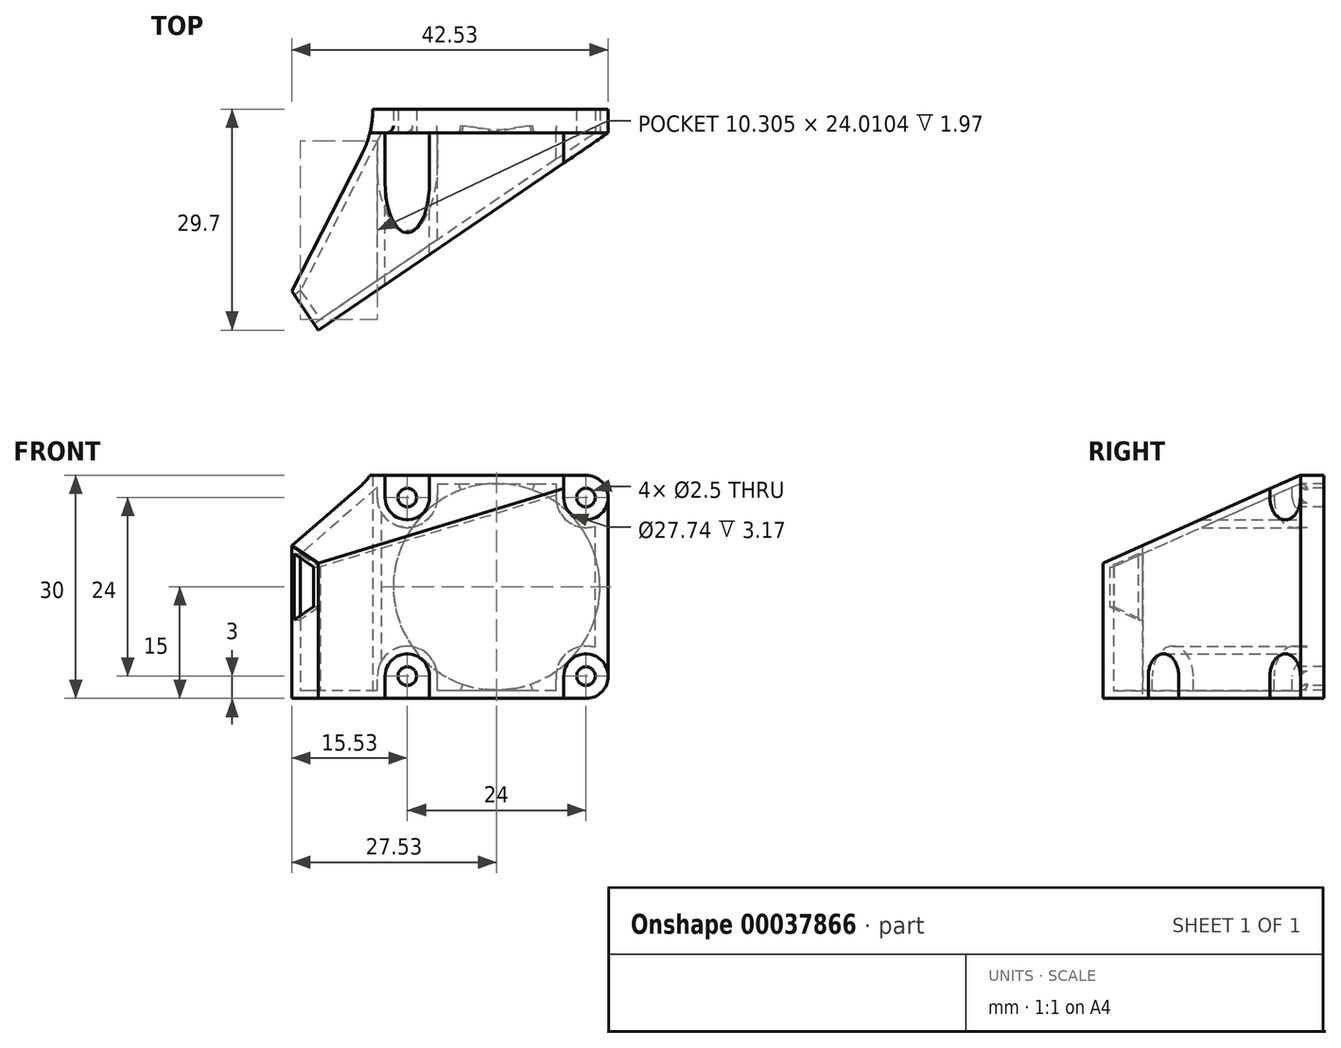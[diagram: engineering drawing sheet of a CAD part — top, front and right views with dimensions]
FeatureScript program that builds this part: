
annotation { "Feature Type Name" : "Feature", "Feature Type Description" : "" }
export const myFeature = defineFeature(function(context is Context, id is Id, definition is map)
    precondition{}
    {
        {
            var Q0;
            Q0=qCreatedBy(makeId("Top.planeOp"),FACE);
            var sketch = newSketch(context, id + "F0", { "sketchPlane" : qUnion([Q0])});
            skLineSegment(sketch, "E0", {"start": v(30, -3.17) * mm, "end": v(-8.96, -29.7) * mm});
            skLineSegment(sketch, "E1", {"start": v(30, 0) * mm, "end": v(0, 0) * mm, "construction": true});
            skLineSegment(sketch, "E2", {"start": v(-1.63, -3.17) * mm, "end": v(-12.53, -24.44) * mm});
            skLineSegment(sketch, "E3", {"start": v(30, 0) * mm, "end": v(30, -3.17) * mm, "construction": true});
            skLineSegment(sketch, "E4", {"start": v(-8.96, -29.7) * mm, "end": v(-12.53, -24.44) * mm});
            skLineSegment(sketch, "E5", {"start": v(30, -3.17) * mm, "end": v(-1.63, -3.17) * mm});
            skLineSegment(sketch, "E6", {"start": v(0, 0) * mm, "end": v(-1.63, -3.17) * mm, "construction": true});
            skSolve(sketch);
        }
        {
            var Q0;
            Q0 = qSketchRegion(id + "F0", true);
            extrude(context, id + "F1", {"entities" : qUnion([Q0]), "depth" : 30 * mm});
        }
        {
            var Q0;
            Q0=qCreatedBy(makeId("Right.planeOp"),FACE);
            var sketch = newSketch(context, id + "F2", { "sketchPlane" : qUnion([Q0])});
            skLineSegment(sketch, "E7.bottom", {"start": v(-3.18, 30) * mm, "end": v(-29.7, 30) * mm});
            skLineSegment(sketch, "E7.top", {"start": v(-3.18, 18.17) * mm, "end": v(-29.7, 18.17) * mm, "construction": true});
            skLineSegment(sketch, "E7.left", {"start": v(-3.18, 30) * mm, "end": v(-3.18, 18.18) * mm, "construction": true});
            skLineSegment(sketch, "E7.right", {"start": v(-29.7, 30) * mm, "end": v(-29.7, 18.17) * mm});
            skLineSegment(sketch, "E8.bottom", {"start": v(-3.18, 0) * mm, "end": v(-29.7, 0) * mm});
            skLineSegment(sketch, "E8.top", {"start": v(-3.18, 11.82) * mm, "end": v(-29.7, 11.82) * mm, "construction": true});
            skLineSegment(sketch, "E8.left", {"start": v(-3.18, 0) * mm, "end": v(-3.18, 11.82) * mm, "construction": true});
            skLineSegment(sketch, "E8.right", {"start": v(-29.7, 0) * mm, "end": v(-29.7, 11.82) * mm});
            skLineSegment(sketch, "E9", {"start": v(-3.18, 30) * mm, "end": v(-29.7, 18.17) * mm});
            skLineSegment(sketch, "E10", {"start": v(-29.7, 11.83) * mm, "end": v(-3.18, 0) * mm});
            skSolve(sketch);
        }
        {
            var Q0;
            Q0 = qSketchRegion(id + "F2", true);
            var Q1;
            Q1=makeQuery(id+"F1.opExtrude","SWEPT_FACE",FACE,{"disambiguationData":[OSD([sQuery(id+"F0.wireOp",EDGE,"E0")])]});
            var Q2;
            Q2=makeQuery(id+"F1.opExtrude","SWEPT_FACE",FACE,{"disambiguationData":[OSD([sQuery(id+"F0.wireOp",EDGE,"E2")])]});
            extrude(context, id + "F3", {"entities" : qUnion([Q0]), "operationType" : NewBodyOperationType.REMOVE, "endBound" : BoundingType.UP_TO_SURFACE, "endBoundEntityFace" : qUnion([Q1]), "depth" : 25.4 * mm, "hasSecondDirection" : true, "secondDirectionBound" : SecondDirectionBoundingType.UP_TO_SURFACE, "secondDirectionOppositeDirection" : true, "secondDirectionBoundEntityFace" : qUnion([Q2]), "secondDirectionDepth" : 25.4 * mm});
        }
        {
            var Q0;
            Q0=makeQuery(id+"F1.opExtrude","SWEPT_FACE",FACE,{"disambiguationData":[OSD([sQuery(id+"F0.wireOp",EDGE,"E5")])]});
            var sketch = newSketch(context, id + "F4", { "sketchPlane" : qUnion([Q0])});
            skLineSegment(sketch, "E11.bottom", {"start": v(-30, 0) * mm, "end": v(-24, 0) * mm});
            skLineSegment(sketch, "E11.top", {"start": v(-30, 3) * mm, "end": v(-24, 3) * mm, "construction": true});
            skLineSegment(sketch, "E11.left", {"start": v(-30, 0) * mm, "end": v(-30, 3) * mm});
            skLineSegment(sketch, "E11.right", {"start": v(-24, 0) * mm, "end": v(-24, 3) * mm});
            skLineSegment(sketch, "E12.bottom", {"start": v(-30, 30) * mm, "end": v(-24, 30) * mm});
            skLineSegment(sketch, "E12.top", {"start": v(-30, 27) * mm, "end": v(-24, 27) * mm, "construction": true});
            skLineSegment(sketch, "E12.left", {"start": v(-30, 30) * mm, "end": v(-30, 27) * mm});
            skLineSegment(sketch, "E12.right", {"start": v(-24, 30) * mm, "end": v(-24, 27) * mm});
            skLineSegment(sketch, "E13.bottom", {"start": v(-27, 27) * mm, "end": v(-3, 27) * mm, "construction": true});
            skLineSegment(sketch, "E13.top", {"start": v(-27, 3) * mm, "end": v(-3, 3) * mm, "construction": true});
            skLineSegment(sketch, "E13.left", {"start": v(-27, 27) * mm, "end": v(-27, 3) * mm, "construction": true});
            skLineSegment(sketch, "E13.right", {"start": v(-3, 27) * mm, "end": v(-3, 3) * mm, "construction": true});
            skPoint(sketch, "E14.rect.middle", {"position": v(-3, 3) * mm});
            skPoint(sketch, "E15.rect.middle", {"position": v(-3, 27) * mm});
            skLineSegment(sketch, "E16.bottom", {"start": v(0, 30) * mm, "end": v(-6, 30) * mm});
            skLineSegment(sketch, "E16.top", {"start": v(0, 27) * mm, "end": v(-6, 27) * mm, "construction": true});
            skLineSegment(sketch, "E16.left", {"start": v(0, 30) * mm, "end": v(0, 27) * mm});
            skLineSegment(sketch, "E16.right", {"start": v(-6, 30) * mm, "end": v(-6, 27) * mm});
            skLineSegment(sketch, "E17.bottom", {"start": v(0, 0) * mm, "end": v(-6, 0) * mm});
            skLineSegment(sketch, "E17.top", {"start": v(0, 3) * mm, "end": v(-6, 3) * mm, "construction": true});
            skLineSegment(sketch, "E17.left", {"start": v(0, 0) * mm, "end": v(0, 3) * mm});
            skLineSegment(sketch, "E17.right", {"start": v(-6, 0) * mm, "end": v(-6, 3) * mm});
            skArc(sketch, "E18", {"start": v(0, 3) * mm, "mid": v(-3, 6) * mm, "end": v(-6, 3) * mm});
            skArc(sketch, "E19", {"start": v(-6, 27) * mm, "mid": v(-3, 24) * mm, "end": v(0, 27) * mm});
            skArc(sketch, "E20", {"start": v(-24, 3) * mm, "mid": v(-27, 6) * mm, "end": v(-30, 3) * mm});
            skArc(sketch, "E21", {"start": v(-30, 27) * mm, "mid": v(-27, 24) * mm, "end": v(-24, 27) * mm});
            skSolve(sketch);
        }
        {
            var Q0;
            Q0 = qSketchRegion(id + "F4", true);
            var Q1;
            Q1=makeQuery(id+"F1.opExtrude","SWEPT_FACE",FACE,{"disambiguationData":[OSD([sQuery(id+"F0.wireOp",EDGE,"E0")])]});
            extrude(context, id + "F5", {"entities" : qUnion([Q0]), "operationType" : NewBodyOperationType.REMOVE, "endBound" : BoundingType.UP_TO_SURFACE, "oppositeDirection" : true, "endBoundEntityFace" : qUnion([Q1]), "depth" : 101.6 * mm});
        }
        {
            var Q0;
            Q0=makeQuery(id+"F1.opExtrude","SWEPT_FACE",FACE,{"disambiguationData":[OSD([sQuery(id+"F0.wireOp",EDGE,"E5")])]});
            shell(context, id + "F6", {"entities" : qUnion([Q0]), "thickness" : 1.03 * mm});
        }
        {
            var Q0;
            Q0=makeQuery(id+"F6.opShell","OFFSET_FACE",FACE,{"disambiguationData":[OSD([sQuery(id+"F0.wireOp",EDGE,"E4")])]});
            var sketch = newSketch(context, id + "F7", { "sketchPlane" : qUnion([Q0])});
            skLineSegment(sketch, "E22", {"start": v(-18.48, 12.31) * mm, "end": v(-13.77, 10.58) * mm});
            skLineSegment(sketch, "E23", {"start": v(-13.77, 10.58) * mm, "end": v(-13.77, 19.42) * mm});
            skLineSegment(sketch, "E24", {"start": v(-13.77, 19.42) * mm, "end": v(-18.48, 17.69) * mm});
            skLineSegment(sketch, "E25", {"start": v(-18.48, 17.69) * mm, "end": v(-18.48, 12.31) * mm});
            skSolve(sketch);
        }
        {
            var Q0;
            Q0 = qSketchRegion(id + "F7", true);
            var Q1;
            Q1=makeQuery(id+"F1.opExtrude","SWEPT_FACE",FACE,{"disambiguationData":[OSD([sQuery(id+"F0.wireOp",EDGE,"E4")])]});
            extrude(context, id + "F8", {"entities" : qUnion([Q0]), "operationType" : NewBodyOperationType.REMOVE, "endBound" : BoundingType.UP_TO_SURFACE, "oppositeDirection" : true, "endBoundEntityFace" : qUnion([Q1]), "depth" : 25.4 * mm});
        }
        {
            var Q0;
            Q0=makeQuery(id+"F1.opExtrude","SWEPT_FACE",FACE,{"disambiguationData":[OSD([sQuery(id+"F0.wireOp",EDGE,"E5")])]});
            var sketch = newSketch(context, id + "F9", { "sketchPlane" : qUnion([Q0])});
            skLineSegment(sketch, "E26.bottom", {"start": v(-30, 0) * mm, "end": v(1.63, 0) * mm});
            skLineSegment(sketch, "E26.top", {"start": v(-30, 30) * mm, "end": v(1.63, 30) * mm});
            skLineSegment(sketch, "E26.left", {"start": v(-30, 0) * mm, "end": v(-30, 30) * mm});
            skLineSegment(sketch, "E26.right", {"start": v(1.63, 0) * mm, "end": v(1.63, 30) * mm});
            skCircle(sketch, "E27", {"center": v(-15, 15) * mm, "radius": 13.87 * mm});
            skLineSegment(sketch, "E28", {"start": v(-30, 15) * mm, "end": v(0, 15) * mm, "construction": true});
            skCircle(sketch, "E29", {"center": v(-27, 27) * mm, "radius": 1.25 * mm});
            skCircle(sketch, "E30", {"center": v(-3, 27) * mm, "radius": 1.25 * mm});
            skCircle(sketch, "E31", {"center": v(-3, 3) * mm, "radius": 1.25 * mm});
            skCircle(sketch, "E32", {"center": v(-27, 3) * mm, "radius": 1.25 * mm});
            skSolve(sketch);
        }
        {
            var Q0;
            Q0 = qSketchRegion(id + "F9", true);
            extrude(context, id + "F10", {"entities" : qUnion([Q0]), "operationType" : NewBodyOperationType.ADD, "depth" : 3.17 * mm});
        }
        {
            var Q0;
            {var subQ0=sQuery(id+"F9.wireOp",EDGE,"E27");Q0=makeQuery(id+"F10.boolean.opBoolean","SPLIT",EDGE,{"disambiguationData":[TD([makeQuery(id+"F1.opExtrude","SWEPT_FACE",FACE,{"disambiguationData":[OSD([sQuery(id+"F0.wireOp",EDGE,"E5")])]}),makeQuery(id+"F6.opShell","OFFSET_FACE",FACE,{"disambiguationData":[OSD([sQuery(id+"F4.wireOp",EDGE,"E12.top"),sQuery(id+"F4.wireOp",EDGE,"E12.right")])]}),makeQuery(id+"F4WnS3BjE1bxDX6_1.opExtrude","SWEPT_FACE",FACE,{"disambiguationData":[OSD([sQuery(id+"FhIQt7G3bNc5ZOU_1.wireOp",EDGE,"86a9f358-4fdf-4d32-afb8-8f7dce24b08c.bottom")])]}),makeQuery(id+"F10.opExtrude","CAP_FACE",FACE,{"disambiguationData":[OSD([sQuery(id+"F9.wireOp",EDGE,"E26.bottom"),sQuery(id+"F9.wireOp",EDGE,"E26.top"),sQuery(id+"F9.wireOp",EDGE,"E26.left"),sQuery(id+"F9.wireOp",EDGE,"E26.right"),subQ0,sQuery(id+"F9.wireOp",EDGE,"E29"),sQuery(id+"F9.wireOp",EDGE,"E30"),sQuery(id+"F9.wireOp",EDGE,"E31"),sQuery(id+"F9.wireOp",EDGE,"E32")])],"isStart":true}),makeQuery(id+"F10.opExtrude","SWEPT_FACE",FACE,{"disambiguationData":[OSD([subQ0])]})])],"derivedFrom":makeQuery(id+"F10.opExtrude","CAP_EDGE",EDGE,{"disambiguationData":[OSD([subQ0])],"isStart":true})});}
            var Q1;
            {var subQ0=sQuery(id+"F9.wireOp",EDGE,"E27");Q1=makeQuery(id+"F10.boolean.opBoolean","SPLIT",EDGE,{"disambiguationData":[TD([makeQuery(id+"F1.opExtrude","SWEPT_FACE",FACE,{"disambiguationData":[OSD([sQuery(id+"F0.wireOp",EDGE,"E5")])]}),makeQuery(id+"F6.opShell","OFFSET_FACE",FACE,{"disambiguationData":[OSD([sQuery(id+"F4.wireOp",EDGE,"E11.top"),sQuery(id+"F4.wireOp",EDGE,"E11.right")])]}),makeQuery(id+"F4WnS3BjE1bxDX6_1.opExtrude","SWEPT_FACE",FACE,{"disambiguationData":[OSD([sQuery(id+"FhIQt7G3bNc5ZOU_1.wireOp",EDGE,"86a9f358-4fdf-4d32-afb8-8f7dce24b08c.bottom")])]}),makeQuery(id+"F10.opExtrude","CAP_FACE",FACE,{"disambiguationData":[OSD([sQuery(id+"F9.wireOp",EDGE,"E26.bottom"),sQuery(id+"F9.wireOp",EDGE,"E26.top"),sQuery(id+"F9.wireOp",EDGE,"E26.left"),sQuery(id+"F9.wireOp",EDGE,"E26.right"),subQ0,sQuery(id+"F9.wireOp",EDGE,"E29"),sQuery(id+"F9.wireOp",EDGE,"E30"),sQuery(id+"F9.wireOp",EDGE,"E31"),sQuery(id+"F9.wireOp",EDGE,"E32")])],"isStart":true}),makeQuery(id+"F10.opExtrude","SWEPT_FACE",FACE,{"disambiguationData":[OSD([subQ0])]})])],"derivedFrom":makeQuery(id+"F10.opExtrude","CAP_EDGE",EDGE,{"disambiguationData":[OSD([subQ0])],"isStart":true})});}
            var Q2;
            {var subQ0=sQuery(id+"F9.wireOp",EDGE,"E27");Q2=makeQuery(id+"F10.boolean.opBoolean","SPLIT",EDGE,{"disambiguationData":[TD([makeQuery(id+"F1.opExtrude","SWEPT_FACE",FACE,{"disambiguationData":[OSD([sQuery(id+"F0.wireOp",EDGE,"E5")])]}),makeQuery(id+"F6.opShell","OFFSET_FACE",FACE,{"disambiguationData":[OSD([sQuery(id+"F4.wireOp",EDGE,"E14.rect.top"),sQuery(id+"F4.wireOp",EDGE,"E14.rect.left")])]}),makeQuery(id+"F10.opExtrude","CAP_FACE",FACE,{"disambiguationData":[OSD([sQuery(id+"F9.wireOp",EDGE,"E26.bottom"),sQuery(id+"F9.wireOp",EDGE,"E26.top"),sQuery(id+"F9.wireOp",EDGE,"E26.left"),sQuery(id+"F9.wireOp",EDGE,"E26.right"),subQ0,sQuery(id+"F9.wireOp",EDGE,"E29"),sQuery(id+"F9.wireOp",EDGE,"E30"),sQuery(id+"F9.wireOp",EDGE,"E31"),sQuery(id+"F9.wireOp",EDGE,"E32")])],"isStart":true}),makeQuery(id+"F10.opExtrude","SWEPT_FACE",FACE,{"disambiguationData":[OSD([subQ0])]})])],"derivedFrom":makeQuery(id+"F10.opExtrude","CAP_EDGE",EDGE,{"disambiguationData":[OSD([subQ0])],"isStart":true})});}
            var Q3;
            {var subQ0=sQuery(id+"F9.wireOp",EDGE,"E27");Q3=makeQuery(id+"F10.boolean.opBoolean","SPLIT",EDGE,{"disambiguationData":[TD([makeQuery(id+"F1.opExtrude","SWEPT_FACE",FACE,{"disambiguationData":[OSD([sQuery(id+"F0.wireOp",EDGE,"E5")])]}),makeQuery(id+"F6.opShell","OFFSET_FACE",FACE,{"disambiguationData":[OSD([sQuery(id+"F4.wireOp",EDGE,"E15.rect.bottom"),sQuery(id+"F4.wireOp",EDGE,"E15.rect.left")])]}),makeQuery(id+"F10.opExtrude","CAP_FACE",FACE,{"disambiguationData":[OSD([sQuery(id+"F9.wireOp",EDGE,"E26.bottom"),sQuery(id+"F9.wireOp",EDGE,"E26.top"),sQuery(id+"F9.wireOp",EDGE,"E26.left"),sQuery(id+"F9.wireOp",EDGE,"E26.right"),subQ0,sQuery(id+"F9.wireOp",EDGE,"E29"),sQuery(id+"F9.wireOp",EDGE,"E30"),sQuery(id+"F9.wireOp",EDGE,"E31"),sQuery(id+"F9.wireOp",EDGE,"E32")])],"isStart":true}),makeQuery(id+"F10.opExtrude","SWEPT_FACE",FACE,{"disambiguationData":[OSD([subQ0])]})])],"derivedFrom":makeQuery(id+"F10.opExtrude","CAP_EDGE",EDGE,{"disambiguationData":[OSD([subQ0])],"isStart":true})});}
            fillet(context, id + "F11", {"entities" : qUnion([Q0, Q1, Q2, Q3]), "radius" : 0.93 * mm, "tangentPropagation" : true, "allowEdgeOverflow" : false});
        }
        {
            var Q0;
            Q0=makeQuery(id+"F10.opExtrude","SWEPT_EDGE",EDGE,{"disambiguationData":[OSD([sQuery(id+"F9.wireOp",EDGE,"E26.top"),sQuery(id+"F9.wireOp",EDGE,"E26.left")])]});
            var Q1;
            Q1=makeQuery(id+"F10.opExtrude","SWEPT_EDGE",EDGE,{"disambiguationData":[OSD([sQuery(id+"F9.wireOp",EDGE,"E26.bottom"),sQuery(id+"F9.wireOp",EDGE,"E26.left")])]});
            fillet(context, id + "F12", {"entities" : qUnion([Q0, Q1]), "radius" : 3 * mm, "tangentPropagation" : true, "allowEdgeOverflow" : false});
        }
        {
            var Q0;
            Q0=makeQuery(id+"F10.boolean.opBoolean","MERGE",EDGE,{"derivedFrom":[makeQuery(id+"F1.opExtrude","SWEPT_EDGE",EDGE,{"disambiguationData":[OSD([sQuery(id+"F0.wireOp",EDGE,"E2"),sQuery(id+"F0.wireOp",EDGE,"E5")])]}),makeQuery(id+"F10.opExtrude","CAP_EDGE",EDGE,{"disambiguationData":[OSD([sQuery(id+"F9.wireOp",EDGE,"E26.right")])],"isStart":true})]});
            fillet(context, id + "F13", {"entities" : qUnion([Q0]), "radius" : 13.15 * mm, "tangentPropagation" : true, "allowEdgeOverflow" : false});
        }
    });
